# Revit family: QF_TRUE_GDM-07-S-HC-TSL01_cat
name_source: partatom
category: Specialty Equipment
revit_build: Autodesk Revit 2015 (Build: 20140606_1530(x64)
units: mm (PartAtom-declared; Revit-internal decimal feet)

## types (1)
- QF_TRUE_GDM-07-S-HC-TSL01_cat
    Apparent Power = 0 VA
    Conn Conduit = Yes
    Conn Plug = NEMA 5-15P
    Cycle = 60 Hz
    Depth = 26 19/32"
    Description = SWING DOOR COUNTER-TOP STAINLESS STEEL REFRIGERATOR WITH HYDROCARBON REFRIGERANT-TRUE STANDARD LOOK VERSION 01
    Elec Conn Connection Height = 0"
    Elec Conn RI Height = 0"
    FL Amps = 2 A
    Foodservice Equipment Identifier = Yes
    HP = 1/6
    Height = 39 25/32"
    Identify Quantity as Lot = Yes
    Length = 24 1/32"
    Manufacturer = TRUE
    Max Overcurrent Protection = 0 A
    Min Ckt Ampacity = 0 A
    Model = GDM-07-S-HC-TSL01
    Number of Poles = 1
    Phase = 1
    Volts = 115 V
    Watts = 219 W
    Weight in Pounds = 0

## geometry (parser evidence)
native form markers: Blend x4, Sweep x1
no freeform markers — native parametric forms only
